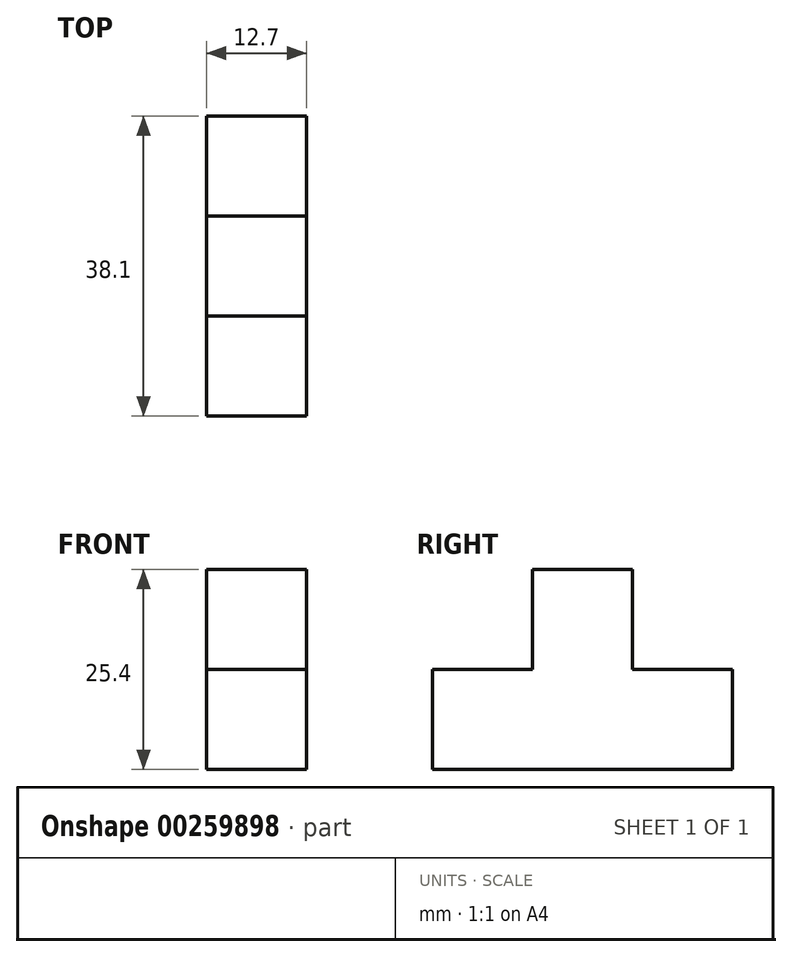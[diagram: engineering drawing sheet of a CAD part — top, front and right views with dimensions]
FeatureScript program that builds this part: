
annotation { "Feature Type Name" : "Feature", "Feature Type Description" : "" }
export const myFeature = defineFeature(function(context is Context, id is Id, definition is map)
    precondition{}
    {
        {
            var Q0;
            Q0=qCreatedBy(makeId("Right.planeOp"),FACE);
            var sketch = newSketch(context, id + "F0", { "sketchPlane" : qUnion([Q0])});
            skLineSegment(sketch, "E0", {"start": v(0, 0) * mm, "end": v(38.1, 0) * mm});
            skLineSegment(sketch, "E1", {"start": v(38.1, 0) * mm, "end": v(38.1, 12.7) * mm});
            skLineSegment(sketch, "E2", {"start": v(38.1, 12.7) * mm, "end": v(25.4, 12.7) * mm});
            skLineSegment(sketch, "E3", {"start": v(25.4, 12.7) * mm, "end": v(25.4, 25.4) * mm});
            skLineSegment(sketch, "E4", {"start": v(25.4, 25.4) * mm, "end": v(12.7, 25.4) * mm});
            skLineSegment(sketch, "E5", {"start": v(12.7, 25.4) * mm, "end": v(12.7, 12.7) * mm});
            skLineSegment(sketch, "E6", {"start": v(12.7, 12.7) * mm, "end": v(0, 12.7) * mm});
            skLineSegment(sketch, "E7", {"start": v(0, 12.7) * mm, "end": v(0, 0) * mm});
            skSolve(sketch);
        }
        {
            var Q0;
            Q0 = qSketchRegion(id + "F0", true);
            extrude(context, id + "F1", {"entities" : qUnion([Q0]), "depth" : 12.7 * mm});
        }
    });
